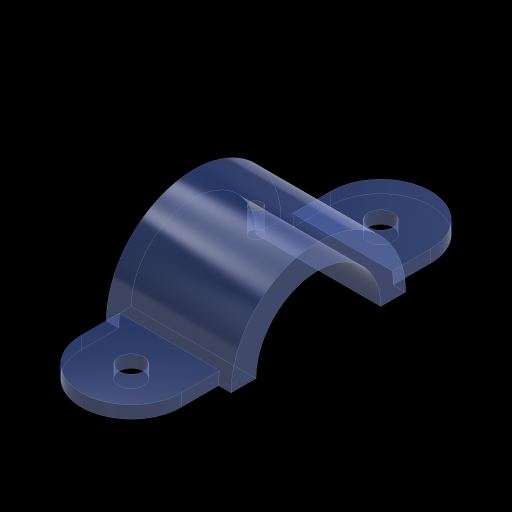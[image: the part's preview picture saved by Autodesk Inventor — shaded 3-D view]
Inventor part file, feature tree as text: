
AUTODESK INVENTOR PART (.ipt)
format: ipt  version: 2024 (Build 280153000, 153)  size: 162,304 bytes
history: native  units: in
note: dims shown in document units (in); Inventor stores cm internally (conversion verified against a paired STEP export)
features: extrude x4, sketch x3
ambient origin geometry x8: Origin, YZ Plane, XZ Plane, XY Plane, X Axis, Y Axis, Z Axis, Center Point
bodies: Solid1 (feature_tree)
feature tree (7):
  extrude  "BASE"  Depth=0.5in
  sketch  "Sketch2"  dims[d2=0.5in d3=1.0in]
  extrude  "REMOVED CENTER OF BASE"  Depth=1.0in
  extrude  "ARCH"  Depth=1.75in
  extrude  "TOPHOLE"  Depth=2.5in
  sketch  "Sketch1"  dims[d0=5.0in d1=0.5in]
  sketch  "Sketch3"  dims[d5=0.25in d6=0.0in d7=1.75in d8=1.25in d9=0.0in d10=0.0in d11=2.5in d12=0.0in d13=0.25in d14=0.0in d15=0.0in]
